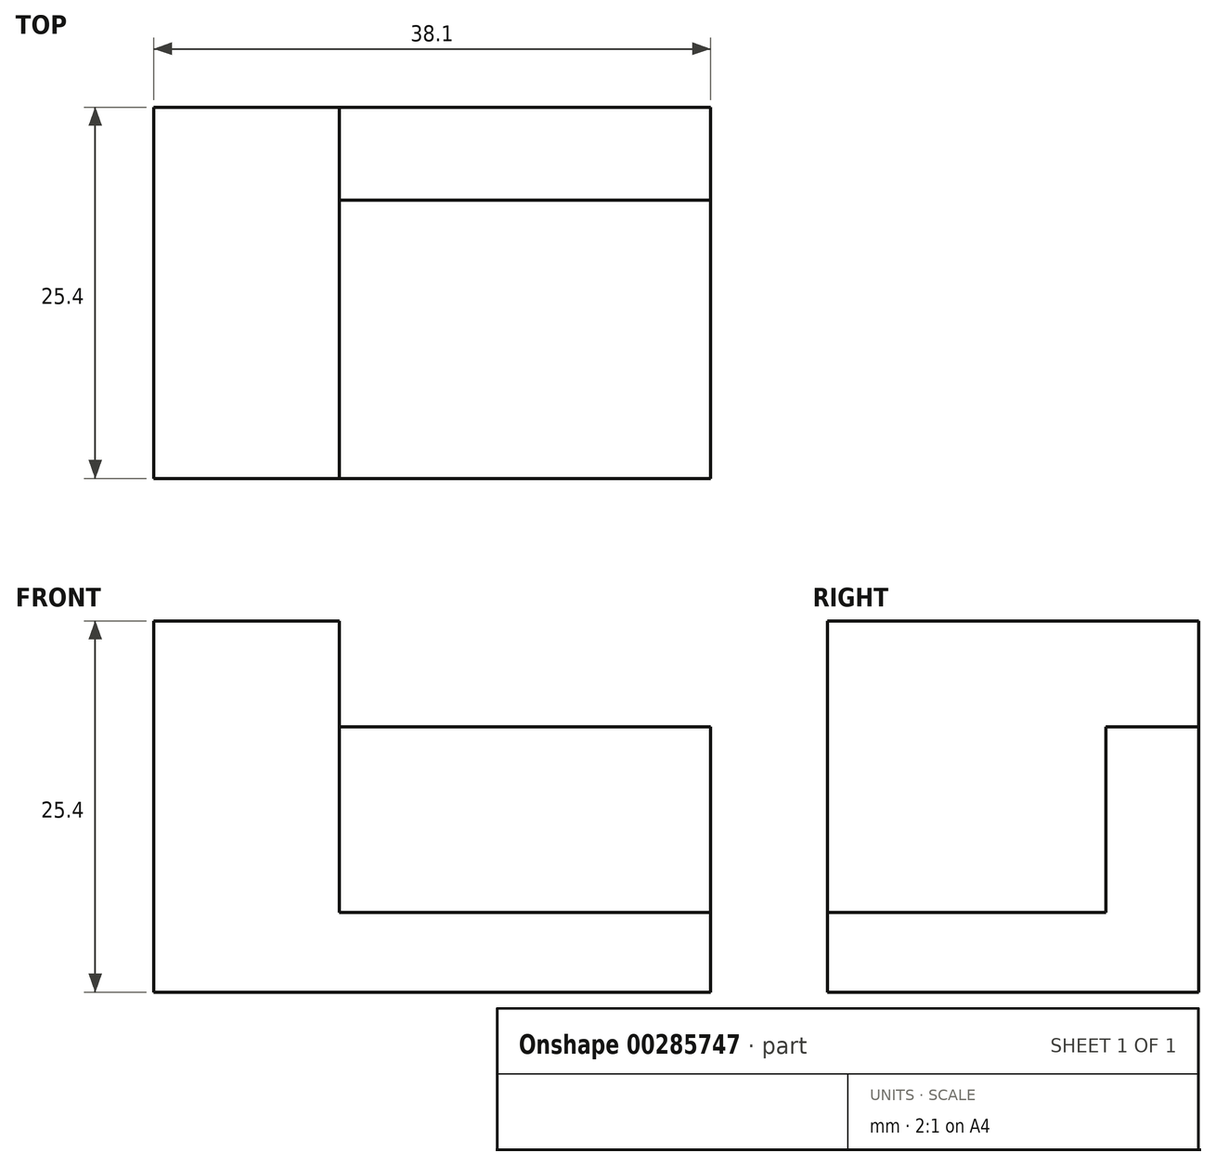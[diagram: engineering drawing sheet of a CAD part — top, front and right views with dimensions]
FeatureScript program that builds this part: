
annotation { "Feature Type Name" : "Feature", "Feature Type Description" : "" }
export const myFeature = defineFeature(function(context is Context, id is Id, definition is map)
    precondition{}
    {
        {
            var Q0;
            Q0=qCreatedBy(makeId("Front.planeOp"),FACE);
            var sketch = newSketch(context, id + "F0", { "sketchPlane" : qUnion([Q0])});
            skLineSegment(sketch, "E0", {"start": v(0, 0) * mm, "end": v(0, 25.4) * mm});
            skLineSegment(sketch, "E1", {"start": v(0, 25.4) * mm, "end": v(12.7, 25.4) * mm});
            skLineSegment(sketch, "E2", {"start": v(12.7, 25.4) * mm, "end": v(12.7, 5.45) * mm});
            skLineSegment(sketch, "E3", {"start": v(12.7, 5.45) * mm, "end": v(38.1, 5.45) * mm});
            skLineSegment(sketch, "E4", {"start": v(38.1, 5.45) * mm, "end": v(38.1, 0) * mm});
            skLineSegment(sketch, "E5", {"start": v(38.1, 0) * mm, "end": v(0, 0) * mm});
            skSolve(sketch);
        }
        {
            var Q0;
            Q0 = qSketchRegion(id + "F0", true);
            extrude(context, id + "F1", {"entities" : qUnion([Q0]), "depth" : 25.4 * mm});
        }
        {
            var Q0;
            Q0=makeQuery(id+"F1.opExtrude","CAP_FACE",FACE,{"disambiguationData":[OSD([sQuery(id+"F0.wireOp",EDGE,"E0"),sQuery(id+"F0.wireOp",EDGE,"E1"),sQuery(id+"F0.wireOp",EDGE,"E2"),sQuery(id+"F0.wireOp",EDGE,"E3"),sQuery(id+"F0.wireOp",EDGE,"E4"),sQuery(id+"F0.wireOp",EDGE,"E5")])],"isStart":true});
            var sketch = newSketch(context, id + "F2", { "sketchPlane" : qUnion([Q0])});
            skLineSegment(sketch, "E6", {"start": v(-38.1, 5.45) * mm, "end": v(-38.1, 18.15) * mm});
            skLineSegment(sketch, "E7", {"start": v(-38.1, 18.15) * mm, "end": v(-12.7, 18.15) * mm});
            skSolve(sketch);
        }
        {
            var Q0;
            Q0 = qSketchRegion(id + "F2", true);
            var Q1;
            Q1=makeQuery(id+"F2.imprint","IMPRINT",FACE,{"disambiguationData":[TD([[makeQuery(id+"F2.imprint","IMPRINT",EDGE,{"derivedFrom":sQuery(id+"F2.wireOp",EDGE,"E6")}),-1.0]])]});
            extrude(context, id + "F3", {"entities" : qUnion([Q0, Q1]), "operationType" : NewBodyOperationType.ADD, "oppositeDirection" : true, "depth" : 6.35 * mm});
        }
    });
